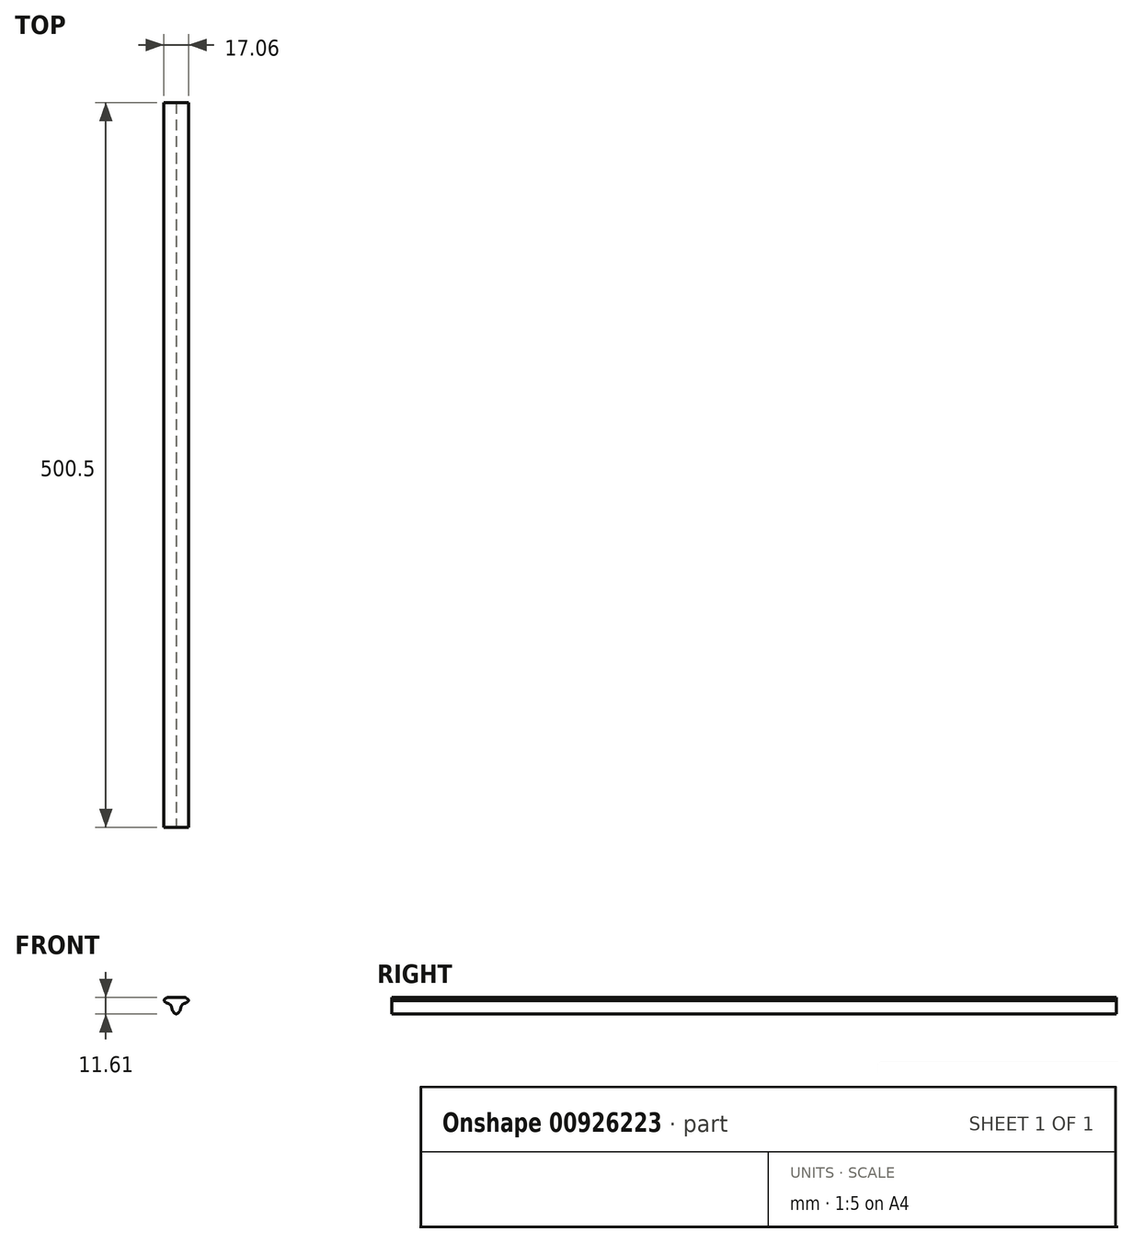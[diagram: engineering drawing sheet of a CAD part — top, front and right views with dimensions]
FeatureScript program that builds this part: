
annotation { "Feature Type Name" : "Feature", "Feature Type Description" : "" }
export const myFeature = defineFeature(function(context is Context, id is Id, definition is map)
    precondition{}
    {
        {
            var Q0;
            Q0=qCreatedBy(makeId("Front.planeOp"),FACE);
            var sketch = newSketch(context, id + "F0", { "sketchPlane" : qUnion([Q0])});
            skLineSegment(sketch, "E0", {"start": v(0, 0) * mm, "end": v(9, 0) * mm});
            skLineSegment(sketch, "E1", {"start": v(9, 0) * mm, "end": v(9, -4) * mm});
            skLineSegment(sketch, "E2", {"start": v(9, -4) * mm, "end": v(3, -4) * mm});
            skLineSegment(sketch, "E3", {"start": v(3, -4) * mm, "end": v(3, -12) * mm});
            skLineSegment(sketch, "E4.MirrorCS", {"start": v(0, 0) * mm, "end": v(-9, 0) * mm});
            skLineSegment(sketch, "E5.MirrorCS", {"start": v(-9, 0) * mm, "end": v(-9, -4) * mm});
            skLineSegment(sketch, "E6.MirrorCS", {"start": v(-9, -4) * mm, "end": v(-3, -4) * mm});
            skLineSegment(sketch, "E7.MirrorCS", {"start": v(-3, -4) * mm, "end": v(-3, -12) * mm});
            skLineSegment(sketch, "E8", {"start": v(-3, -12) * mm, "end": v(3, -12) * mm});
            skSolve(sketch);
        }
        {
            var Q0;
            Q0=makeQuery(id+"F0.imprint","IMPRINT",FACE,{"disambiguationData":[TD([[makeQuery(id+"F0.imprint","IMPRINT",EDGE,{"derivedFrom":sQuery(id+"F0.wireOp",EDGE,"E0")}),-1.0]])]});
            extrude(context, id + "F1", {"entities" : qUnion([Q0]), "depth" : 500.5 * mm, "offsetDistance" : 25 * mm});
        }
        {
            var Q0;
            Q0=makeQuery(id+"F1.opExtrude","SWEPT_EDGE",EDGE,{"disambiguationData":[OSD([sQuery(id+"F0.wireOp",EDGE,"E2"),sQuery(id+"F0.wireOp",EDGE,"E3")])]});
            var Q1;
            Q1=makeQuery(id+"F1.opExtrude","SWEPT_EDGE",EDGE,{"disambiguationData":[OSD([sQuery(id+"F0.wireOp",EDGE,"E6.MirrorCS"),sQuery(id+"F0.wireOp",EDGE,"E7.MirrorCS")])]});
            fillet(context, id + "F2", {"entities" : qUnion([Q0, Q1]), "radius" : 4 * mm, "tangentPropagation" : true, "allowEdgeOverflow" : false});
        }
        {
            var Q0;
            Q0=makeQuery(id+"F1.opExtrude","SWEPT_EDGE",EDGE,{"disambiguationData":[OSD([sQuery(id+"F0.wireOp",EDGE,"E4.MirrorCS"),sQuery(id+"F0.wireOp",EDGE,"E5.MirrorCS")])]});
            var Q1;
            Q1=makeQuery(id+"F1.opExtrude","SWEPT_EDGE",EDGE,{"disambiguationData":[OSD([sQuery(id+"F0.wireOp",EDGE,"E0"),sQuery(id+"F0.wireOp",EDGE,"E1")])]});
            var Q2;
            Q2=makeQuery(id+"F1.opExtrude","SWEPT_EDGE",EDGE,{"disambiguationData":[OSD([sQuery(id+"F0.wireOp",EDGE,"E5.MirrorCS"),sQuery(id+"F0.wireOp",EDGE,"E6.MirrorCS")])]});
            var Q3;
            Q3=makeQuery(id+"F1.opExtrude","SWEPT_EDGE",EDGE,{"disambiguationData":[OSD([sQuery(id+"F0.wireOp",EDGE,"E1"),sQuery(id+"F0.wireOp",EDGE,"E2")])]});
            fillet(context, id + "F3", {"entities" : qUnion([Q0, Q1, Q2, Q3]), "radius" : 4 * mm, "tangentPropagation" : true, "allowEdgeOverflow" : false});
        }
        {
            var Q0;
            Q0=makeQuery(id+"F1.opExtrude","SWEPT_EDGE",EDGE,{"disambiguationData":[OSD([sQuery(id+"F0.wireOp",EDGE,"E3"),sQuery(id+"F0.wireOp",EDGE,"E8")])]});
            var Q1;
            Q1=makeQuery(id+"F1.opExtrude","SWEPT_EDGE",EDGE,{"disambiguationData":[OSD([sQuery(id+"F0.wireOp",EDGE,"E7.MirrorCS"),sQuery(id+"F0.wireOp",EDGE,"E8")])]});
            fillet(context, id + "F4", {"entities" : qUnion([Q0, Q1]), "radius" : 5 * mm, "tangentPropagation" : true, "allowEdgeOverflow" : false});
        }
    });
